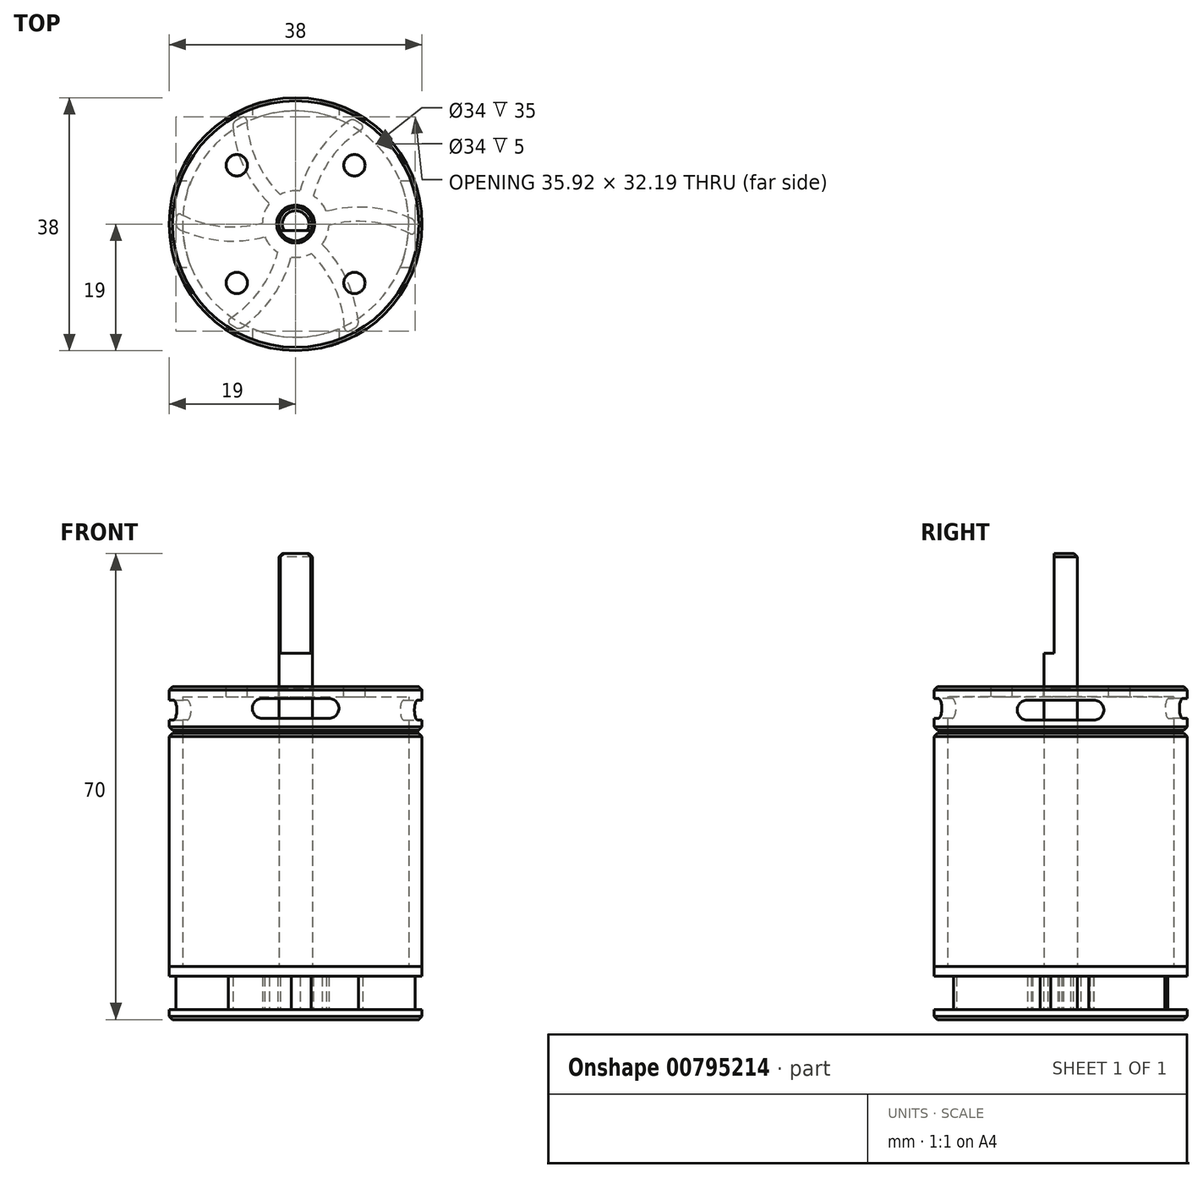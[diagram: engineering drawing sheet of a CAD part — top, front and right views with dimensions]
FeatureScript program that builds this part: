
annotation { "Feature Type Name" : "Feature", "Feature Type Description" : "" }
export const myFeature = defineFeature(function(context is Context, id is Id, definition is map)
    precondition{}
    {
        {
            var Q0;
            Q0=qCreatedBy(makeId("Top.planeOp"),FACE);
            var sketch = newSketch(context, id + "F0", { "sketchPlane" : qUnion([Q0])});
            skCircle(sketch, "E0", {"center": v(0, 0) * mm, "radius": 19 * mm});
            skSolve(sketch);
        }
        {
            var Q0;
            Q0=makeQuery(id+"F0.imprint","IMPRINT",FACE,{"disambiguationData":[TD([[makeQuery(id+"F0.imprint","IMPRINT",EDGE,{"derivedFrom":sQuery(id+"F0.wireOp",EDGE,"E0")}),1.0]])]});
            extrude(context, id + "F1", {"entities" : qUnion([Q0]), "depth" : 1.5 * mm, "offsetDistance" : 25 * mm});
        }
        {
            var Q0;
            Q0=makeQuery(id+"F1.opExtrude","CAP_FACE",FACE,{"disambiguationData":[OSD([sQuery(id+"F0.wireOp",EDGE,"E0")])],"isStart":false});
            var sketch = newSketch(context, id + "F2", { "sketchPlane" : qUnion([Q0])});
            skArc(sketch, "E1", {"start": v(0.66, 4.96) * mm, "mid": v(-0.88, 4.92) * mm, "end": v(-2.33, 4.43) * mm});
            skArc(sketch, "E2.trimOffspring", {"start": v(9.86, 15.01) * mm, "mid": v(9.43, 15.28) * mm, "end": v(9, 15.54) * mm});
            skArc(sketch, "E3.trimOffspring", {"start": v(9.85, 14.17) * mm, "mid": v(5.32, 9.88) * mm, "end": v(2.67, 4.23) * mm});
            skArc(sketch, "E4.trimOffspring", {"start": v(8, 15.5) * mm, "mid": v(3.41, 10.87) * mm, "end": v(0.66, 4.96) * mm});
            skPoint(sketch, "E5.visualSharp", {"position": v(8.49, 15.83) * mm});
            skArc(sketch, "E5.filletArc", {"start": v(9, 15.54) * mm, "mid": v(8.5, 15.67) * mm, "end": v(8, 15.5) * mm});
            skPoint(sketch, "E6.visualSharp", {"position": v(10.5, 14.57) * mm});
            skArc(sketch, "E6.filletArc", {"start": v(9.85, 14.17) * mm, "mid": v(10.08, 14.6) * mm, "end": v(9.86, 15.01) * mm});
            skPoint(sketch, "E7.1.0", {"position": v(-9.46, 15.26) * mm});
            skArc(sketch, "E7.1.1", {"start": v(-9.42, 14.68) * mm, "mid": v(-7.7, 8.4) * mm, "end": v(-3.96, 3.05) * mm});
            skPoint(sketch, "E7.1.2", {"position": v(-7.37, 16.38) * mm});
            skArc(sketch, "E7.1.3", {"start": v(-7.35, 15.62) * mm, "mid": v(-5.9, 9.55) * mm, "end": v(-2.33, 4.43) * mm});
            skArc(sketch, "E7.1.4", {"start": v(-7.35, 15.62) * mm, "mid": v(-7.6, 16.03) * mm, "end": v(-8.07, 16.04) * mm});
            skArc(sketch, "E7.1.5", {"start": v(-8.96, 15.56) * mm, "mid": v(-9.32, 15.19) * mm, "end": v(-9.42, 14.68) * mm});
            skArc(sketch, "E7.1.6", {"start": v(-8.07, 16.04) * mm, "mid": v(-8.52, 15.8) * mm, "end": v(-8.96, 15.56) * mm});
            skPoint(sketch, "E7.2.0", {"position": v(-17.95, -0.56) * mm});
            skArc(sketch, "E7.2.1", {"start": v(-17.43, -0.81) * mm, "mid": v(-11.12, -2.48) * mm, "end": v(-4.62, -1.9) * mm});
            skPoint(sketch, "E7.2.2", {"position": v(-17.87, 1.8) * mm});
            skArc(sketch, "E7.2.3", {"start": v(-17.2, 1.45) * mm, "mid": v(-11.22, -0.33) * mm, "end": v(-5, 0.2) * mm});
            skArc(sketch, "E7.2.4", {"start": v(-17.2, 1.45) * mm, "mid": v(-17.68, 1.43) * mm, "end": v(-17.93, 1.03) * mm});
            skArc(sketch, "E7.2.5", {"start": v(-17.96, 0.02) * mm, "mid": v(-17.81, -0.48) * mm, "end": v(-17.43, -0.81) * mm});
            skArc(sketch, "E7.2.6", {"start": v(-17.93, 1.03) * mm, "mid": v(-17.95, 0.52) * mm, "end": v(-17.96, 0.02) * mm});
            skPoint(sketch, "E7.3.0", {"position": v(-8.49, -15.83) * mm});
            skArc(sketch, "E7.3.1", {"start": v(-8, -15.5) * mm, "mid": v(-3.41, -10.87) * mm, "end": v(-0.66, -4.96) * mm});
            skPoint(sketch, "E7.3.2", {"position": v(-10.5, -14.57) * mm});
            skArc(sketch, "E7.3.3", {"start": v(-9.85, -14.17) * mm, "mid": v(-5.32, -9.88) * mm, "end": v(-2.67, -4.23) * mm});
            skArc(sketch, "E7.3.4", {"start": v(-9.85, -14.17) * mm, "mid": v(-10.08, -14.6) * mm, "end": v(-9.86, -15.01) * mm});
            skArc(sketch, "E7.3.5", {"start": v(-9, -15.54) * mm, "mid": v(-8.5, -15.67) * mm, "end": v(-8, -15.5) * mm});
            skArc(sketch, "E7.3.6", {"start": v(-9.86, -15.01) * mm, "mid": v(-9.43, -15.28) * mm, "end": v(-9, -15.54) * mm});
            skPoint(sketch, "E7.4.0", {"position": v(9.46, -15.26) * mm});
            skArc(sketch, "E7.4.1", {"start": v(9.42, -14.68) * mm, "mid": v(7.7, -8.4) * mm, "end": v(3.96, -3.05) * mm});
            skPoint(sketch, "E7.4.2", {"position": v(7.37, -16.38) * mm});
            skArc(sketch, "E7.4.3", {"start": v(7.35, -15.62) * mm, "mid": v(5.9, -9.55) * mm, "end": v(2.33, -4.43) * mm});
            skArc(sketch, "E7.4.4", {"start": v(7.35, -15.62) * mm, "mid": v(7.6, -16.03) * mm, "end": v(8.07, -16.04) * mm});
            skArc(sketch, "E7.4.5", {"start": v(8.96, -15.56) * mm, "mid": v(9.32, -15.19) * mm, "end": v(9.42, -14.68) * mm});
            skArc(sketch, "E7.4.6", {"start": v(8.07, -16.04) * mm, "mid": v(8.52, -15.8) * mm, "end": v(8.96, -15.56) * mm});
            skPoint(sketch, "E7.5.0", {"position": v(17.95, 0.56) * mm});
            skArc(sketch, "E7.5.1", {"start": v(17.43, 0.81) * mm, "mid": v(11.12, 2.48) * mm, "end": v(4.62, 1.9) * mm});
            skPoint(sketch, "E7.5.2", {"position": v(17.87, -1.8) * mm});
            skArc(sketch, "E7.5.3", {"start": v(17.2, -1.45) * mm, "mid": v(11.22, 0.33) * mm, "end": v(5, -0.2) * mm});
            skArc(sketch, "E7.5.4", {"start": v(17.2, -1.45) * mm, "mid": v(17.68, -1.43) * mm, "end": v(17.93, -1.03) * mm});
            skArc(sketch, "E7.5.5", {"start": v(17.96, -0.02) * mm, "mid": v(17.81, 0.48) * mm, "end": v(17.43, 0.81) * mm});
            skArc(sketch, "E7.5.6", {"start": v(17.93, -1.03) * mm, "mid": v(17.95, -0.52) * mm, "end": v(17.96, -0.02) * mm});
            skArc(sketch, "E8.trimOffspring", {"start": v(-3.96, 3.05) * mm, "mid": v(-4.7, 1.7) * mm, "end": v(-5, 0.2) * mm});
            skArc(sketch, "E9.trimOffspring", {"start": v(-4.62, -1.9) * mm, "mid": v(-3.83, -3.22) * mm, "end": v(-2.67, -4.23) * mm});
            skArc(sketch, "E10.trimOffspring", {"start": v(-0.66, -4.96) * mm, "mid": v(0.88, -4.92) * mm, "end": v(2.33, -4.43) * mm});
            skArc(sketch, "E11.trimOffspring", {"start": v(3.96, -3.05) * mm, "mid": v(4.7, -1.7) * mm, "end": v(5, -0.2) * mm});
            skArc(sketch, "E12.trimOffspring", {"start": v(4.62, 1.9) * mm, "mid": v(3.83, 3.22) * mm, "end": v(2.67, 4.23) * mm});
            skSolve(sketch);
        }
        {
            var Q0;
            Q0 = qSketchRegion(id + "F2", true);
            extrude(context, id + "F3", {"entities" : qUnion([Q0]), "operationType" : NewBodyOperationType.ADD, "depth" : 5 * mm, "offsetDistance" : 25 * mm});
        }
        {
            var Q0;
            Q0=makeQuery(id+"F3.opExtrude","CAP_FACE",FACE,{"disambiguationData":[OSD([sQuery(id+"F2.wireOp",EDGE,"E1"),sQuery(id+"F2.wireOp",EDGE,"E2.trimOffspring"),sQuery(id+"F2.wireOp",EDGE,"E3.trimOffspring"),sQuery(id+"F2.wireOp",EDGE,"E4.trimOffspring"),sQuery(id+"F2.wireOp",EDGE,"E5.filletArc"),sQuery(id+"F2.wireOp",EDGE,"E6.filletArc"),sQuery(id+"F2.wireOp",EDGE,"E7.1.1"),sQuery(id+"F2.wireOp",EDGE,"E7.1.3"),sQuery(id+"F2.wireOp",EDGE,"E7.1.4"),sQuery(id+"F2.wireOp",EDGE,"E7.1.5"),sQuery(id+"F2.wireOp",EDGE,"E7.1.6"),sQuery(id+"F2.wireOp",EDGE,"E7.2.1"),sQuery(id+"F2.wireOp",EDGE,"E7.2.3"),sQuery(id+"F2.wireOp",EDGE,"E7.2.4"),sQuery(id+"F2.wireOp",EDGE,"E7.2.5"),sQuery(id+"F2.wireOp",EDGE,"E7.2.6"),sQuery(id+"F2.wireOp",EDGE,"E7.3.1"),sQuery(id+"F2.wireOp",EDGE,"E7.3.3"),sQuery(id+"F2.wireOp",EDGE,"E7.3.4"),sQuery(id+"F2.wireOp",EDGE,"E7.3.5"),sQuery(id+"F2.wireOp",EDGE,"E7.3.6"),sQuery(id+"F2.wireOp",EDGE,"E7.4.1"),sQuery(id+"F2.wireOp",EDGE,"E7.4.3"),sQuery(id+"F2.wireOp",EDGE,"E7.4.4"),sQuery(id+"F2.wireOp",EDGE,"E7.4.5"),sQuery(id+"F2.wireOp",EDGE,"E7.4.6"),sQuery(id+"F2.wireOp",EDGE,"E7.5.1"),sQuery(id+"F2.wireOp",EDGE,"E7.5.3"),sQuery(id+"F2.wireOp",EDGE,"E7.5.4"),sQuery(id+"F2.wireOp",EDGE,"E7.5.5"),sQuery(id+"F2.wireOp",EDGE,"E7.5.6"),sQuery(id+"F2.wireOp",EDGE,"E8.trimOffspring"),sQuery(id+"F2.wireOp",EDGE,"E9.trimOffspring"),sQuery(id+"F2.wireOp",EDGE,"E10.trimOffspring"),sQuery(id+"F2.wireOp",EDGE,"E11.trimOffspring"),sQuery(id+"F2.wireOp",EDGE,"E12.trimOffspring")])],"isStart":false});
            var sketch = newSketch(context, id + "F4", { "sketchPlane" : qUnion([Q0])});
            skCircle(sketch, "E13", {"center": v(0, 0) * mm, "radius": 19 * mm});
            skSolve(sketch);
        }
        {
            var Q0;
            Q0 = qSketchRegion(id + "F4", true);
            extrude(context, id + "F5", {"entities" : qUnion([Q0]), "operationType" : NewBodyOperationType.ADD, "depth" : 1.5 * mm, "offsetDistance" : 25 * mm});
        }
        {
            var Q0;
            Q0=makeQuery(id+"F1.opExtrude","CAP_EDGE",EDGE,{"disambiguationData":[OSD([sQuery(id+"F0.wireOp",EDGE,"E0")])],"isStart":true});
            chamfer(context, id + "F6", {"entities" : qUnion([Q0]), "width" : .5 * mm, "tangentPropagation" : true});
        }
        {
            var Q0;
            Q0=makeQuery(id+"F5.opExtrude","CAP_FACE",FACE,{"disambiguationData":[OSD([sQuery(id+"F4.wireOp",EDGE,"E13")])],"isStart":false});
            var sketch = newSketch(context, id + "F7", { "sketchPlane" : qUnion([Q0])});
            skCircle(sketch, "E14", {"center": v(0, 0) * mm, "radius": 19 * mm});
            skCircle(sketch, "E15", {"center": v(0, 0) * mm, "radius": 17 * mm});
            skSolve(sketch);
        }
        {
            var Q0;
            Q0 = qSketchRegion(id + "F7", true);
            extrude(context, id + "F8", {"entities" : qUnion([Q0]), "depth" : 35 * mm, "offsetDistance" : 25 * mm});
        }
        {
            var Q0;
            Q0=makeQuery(id+"F8.opExtrude","CAP_FACE",FACE,{"disambiguationData":[OSD([sQuery(id+"F7.wireOp",EDGE,"E14"),sQuery(id+"F7.wireOp",EDGE,"E15")])],"isStart":false});
            cPlane(context, id + "F9", {"entities" : qUnion([Q0]), "cplaneType" : CPlaneType.OFFSET, "offset" : .5 * mm, "width" : 150 * mm, "height" : 150 * mm});
        }
        {
            var Q0;
            Q0=qCreatedBy(id+"F9.planeOp",FACE);
            var sketch = newSketch(context, id + "F10", { "sketchPlane" : qUnion([Q0])});
            skCircle(sketch, "E16", {"center": v(0, 0) * mm, "radius": 19 * mm});
            skSolve(sketch);
        }
        {
            var Q0;
            Q0 = qSketchRegion(id + "F10", true);
            extrude(context, id + "F11", {"entities" : qUnion([Q0]), "depth" : 6.5 * mm, "offsetDistance" : 25 * mm});
        }
        {
            var Q0;
            Q0=makeQuery(id+"F8.opExtrude","CAP_EDGE",EDGE,{"disambiguationData":[OSD([sQuery(id+"F7.wireOp",EDGE,"E14")])],"isStart":false});
            var Q1;
            Q1=makeQuery(id+"F11.opExtrude","CAP_EDGE",EDGE,{"disambiguationData":[OSD([sQuery(id+"F10.wireOp",EDGE,"E16")])],"isStart":true});
            var Q2;
            Q2=makeQuery(id+"F11.opExtrude","CAP_EDGE",EDGE,{"disambiguationData":[OSD([sQuery(id+"F10.wireOp",EDGE,"E16")])],"isStart":false});
            chamfer(context, id + "F12", {"entities" : qUnion([Q0, Q1, Q2]), "width" : .5 * mm, "tangentPropagation" : true});
        }
        {
            var Q0;
            Q0=qCreatedBy(makeId("Front.planeOp"),FACE);
            var sketch = newSketch(context, id + "F13", { "sketchPlane" : qUnion([Q0])});
            skLineSegment(sketch, "E17", {"start": v(-5, 46.75) * mm, "end": v(5, 46.75) * mm, "construction": true});
            skArc(sketch, "E18.0.startCap", {"start": v(-5, 45.25) * mm, "mid": v(-6.5, 46.75) * mm, "end": v(-5, 48.25) * mm});
            skArc(sketch, "E18.0.endCap", {"start": v(5, 48.25) * mm, "mid": v(6.5, 46.75) * mm, "end": v(5, 45.25) * mm});
            skLineSegment(sketch, "E18.0.left", {"start": v(-5, 48.25) * mm, "end": v(5, 48.25) * mm});
            skLineSegment(sketch, "E18.0.right", {"start": v(-5, 45.25) * mm, "end": v(5, 45.25) * mm});
            skSolve(sketch);
        }
        {
            var Q0;
            Q0 = qSketchRegion(id + "F13", true);
            extrude(context, id + "F14", {"entities" : qUnion([Q0]), "operationType" : NewBodyOperationType.REMOVE, "endBound" : BoundingType.SYMMETRIC, "oppositeDirection" : true, "depth" : 75 * mm, "offsetDistance" : 25 * mm});
        }
        {
            var Q0;
            Q0=qCreatedBy(makeId("Right.planeOp"),FACE);
            var sketch = newSketch(context, id + "F15", { "sketchPlane" : qUnion([Q0])});
            skLineSegment(sketch, "E19", {"start": v(5, 46.5) * mm, "end": v(-5, 46.5) * mm});
            skArc(sketch, "E20.0.startCap", {"start": v(5, 48) * mm, "mid": v(6.5, 46.5) * mm, "end": v(5, 45) * mm});
            skArc(sketch, "E20.0.endCap", {"start": v(-5, 45) * mm, "mid": v(-6.5, 46.5) * mm, "end": v(-5, 48) * mm});
            skLineSegment(sketch, "E20.0.left", {"start": v(5, 45) * mm, "end": v(-5, 45) * mm});
            skLineSegment(sketch, "E20.0.right", {"start": v(5, 48) * mm, "end": v(-5, 48) * mm});
            skSolve(sketch);
        }
        {
            var Q0;
            Q0 = qSketchRegion(id + "F15", true);
            extrude(context, id + "F16", {"entities" : qUnion([Q0]), "operationType" : NewBodyOperationType.REMOVE, "endBound" : BoundingType.SYMMETRIC, "oppositeDirection" : true, "depth" : 75 * mm, "offsetDistance" : 25 * mm});
        }
        {
            var Q0;
            Q0=makeQuery(id+"F11.opExtrude","CAP_FACE",FACE,{"disambiguationData":[OSD([sQuery(id+"F10.wireOp",EDGE,"E16")])],"isStart":true});
            var sketch = newSketch(context, id + "F17", { "sketchPlane" : qUnion([Q0])});
            skCircle(sketch, "E21", {"center": v(0, 0) * mm, "radius": 17 * mm});
            skSolve(sketch);
        }
        {
            var Q0;
            Q0=makeQuery(id+"F17.imprint","IMPRINT",FACE,{"disambiguationData":[TD([[makeQuery(id+"F17.imprint","IMPRINT",EDGE,{"derivedFrom":sQuery(id+"F17.wireOp",EDGE,"E21")}),1.0]])]});
            extrude(context, id + "F18", {"entities" : qUnion([Q0]), "operationType" : NewBodyOperationType.REMOVE, "oppositeDirection" : true, "depth" : 5 * mm, "offsetDistance" : 25 * mm});
        }
        {
            var Q0;
            Q0=makeQuery(id+"F5.opExtrude","CAP_FACE",FACE,{"disambiguationData":[OSD([sQuery(id+"F4.wireOp",EDGE,"E13")])],"isStart":false});
            var sketch = newSketch(context, id + "F19", { "sketchPlane" : qUnion([Q0])});
            skCircle(sketch, "E22", {"center": v(0, 0) * mm, "radius": 2.6 * mm});
            skSolve(sketch);
        }
        {
            var Q0;
            Q0=makeQuery(id+"F19.imprint","IMPRINT",FACE,{"disambiguationData":[TD([[makeQuery(id+"F19.imprint","IMPRINT",EDGE,{"derivedFrom":sQuery(id+"F19.wireOp",EDGE,"E22")}),1.0]])]});
            extrude(context, id + "F20", {"entities" : qUnion([Q0]), "operationType" : NewBodyOperationType.REMOVE, "depth" : 45 * mm, "offsetDistance" : 25 * mm});
        }
        {
            var Q0;
            Q0=makeQuery(id+"F20.boolean.opBoolean","INTERSECT",EDGE,{"derivedFrom":[makeQuery(id+"F11.opExtrude","CAP_FACE",FACE,{"disambiguationData":[OSD([sQuery(id+"F10.wireOp",EDGE,"E16")])],"isStart":false}),makeQuery(id+"F20.opExtrude","SWEPT_FACE",FACE,{"disambiguationData":[OSD([sQuery(id+"F19.wireOp",EDGE,"E22")])]})]});
            chamfer(context, id + "F21", {"entities" : qUnion([Q0]), "width" : .25 * mm, "tangentPropagation" : true});
        }
        {
            var Q0;
            Q0=makeQuery(id+"F5.opExtrude","CAP_FACE",FACE,{"disambiguationData":[OSD([sQuery(id+"F4.wireOp",EDGE,"E13")])],"isStart":false});
            var sketch = newSketch(context, id + "F22", { "sketchPlane" : qUnion([Q0])});
            skCircle(sketch, "E23", {"center": v(0, 0) * mm, "radius": 2.5 * mm});
            skSolve(sketch);
        }
        {
            var Q0;
            Q0=makeQuery(id+"F22.imprint","IMPRINT",FACE,{"disambiguationData":[TD([[makeQuery(id+"F22.imprint","IMPRINT",EDGE,{"derivedFrom":sQuery(id+"F22.wireOp",EDGE,"E23")}),1.0]])]});
            extrude(context, id + "F23", {"entities" : qUnion([Q0]), "depth" : 62 * mm, "offsetDistance" : 25 * mm});
        }
        {
            var Q0;
            Q0=makeQuery(id+"F23.opExtrude","CAP_FACE",FACE,{"disambiguationData":[OSD([sQuery(id+"F22.wireOp",EDGE,"E23")])],"isStart":false});
            var sketch = newSketch(context, id + "F24", { "sketchPlane" : qUnion([Q0])});
            skLineSegment(sketch, "E24", {"start": v(-2.5, -1) * mm, "end": v(2.72, -1) * mm});
            skSolve(sketch);
        }
        {
            var Q0;
            Q0=makeQuery(id+"F23.opExtrude","CAP_EDGE",EDGE,{"disambiguationData":[OSD([sQuery(id+"F22.wireOp",EDGE,"E23")])],"isStart":false});
            chamfer(context, id + "F25", {"entities" : qUnion([Q0]), "width" : .5 * mm, "tangentPropagation" : true});
        }
        {
            var Q0;
            {var subQ0=sQuery(id+"F24.wireOp",EDGE,"E24");var subQ1=makeQuery(id+"F23.opExtrude","CAP_EDGE",EDGE,{"disambiguationData":[OSD([sQuery(id+"F22.wireOp",EDGE,"E23")])],"isStart":false});var subQ2=makeQuery(id+"F24.imprint","INTERSECT",VERTEX,{"disambiguationData":[OD(0.0)],"derivedFrom":[subQ1,subQ0]});Q0=makeQuery(id+"F24.imprint","IMPRINT",FACE,{"disambiguationData":[TD([[makeQuery(id+"F24.imprint","IMPRINT",EDGE,{"disambiguationData":[TD([[subQ2,-1.0]])],"derivedFrom":subQ0}),-1.0]])]});}
            extrude(context, id + "F26", {"entities" : qUnion([Q0]), "operationType" : NewBodyOperationType.REMOVE, "oppositeDirection" : true, "depth" : 15 * mm, "offsetDistance" : 25 * mm});
        }
        {
            var Q0;
            {var subQ0=sQuery(id+"F24.wireOp",EDGE,"E24");var subQ1=makeQuery(id+"F23.opExtrude","CAP_EDGE",EDGE,{"disambiguationData":[OSD([sQuery(id+"F22.wireOp",EDGE,"E23")])],"isStart":false});var subQ2=makeQuery(id+"F24.imprint","INTERSECT",VERTEX,{"disambiguationData":[OD(0.0)],"derivedFrom":[subQ1,subQ0]});Q0=makeQuery(id+"F24.imprint","IMPRINT",FACE,{"disambiguationData":[TD([[makeQuery(id+"F24.imprint","IMPRINT",EDGE,{"disambiguationData":[TD([[subQ2,-1.0]])],"derivedFrom":subQ0}),-1.0]])]});}
            extrude(context, id + "F27", {"entities" : qUnion([Q0]), "operationType" : NewBodyOperationType.REMOVE, "oppositeDirection" : true, "depth" : 15 * mm, "offsetDistance" : 25 * mm});
        }
        {
            var Q0;
            Q0=makeQuery(id+"F11.opExtrude","CAP_FACE",FACE,{"disambiguationData":[OSD([sQuery(id+"F10.wireOp",EDGE,"E16")])],"isStart":false});
            var sketch = newSketch(context, id + "F28", { "sketchPlane" : qUnion([Q0])});
            skCircle(sketch, "E25", {"center": v(0, 0) * mm, "radius": 12.5 * mm, "construction": true});
            skLineSegment(sketch, "E26", {"start": v(0, 0) * mm, "end": v(-11.57, 11.57) * mm, "construction": true});
            skCircle(sketch, "E27", {"center": v(-8.84, 8.84) * mm, "radius": 1.6 * mm});
            skCircle(sketch, "E28.1.0", {"center": v(-8.84, -8.84) * mm, "radius": 1.6 * mm});
            skCircle(sketch, "E28.2.0", {"center": v(8.84, -8.84) * mm, "radius": 1.6 * mm});
            skCircle(sketch, "E28.3.0", {"center": v(8.84, 8.84) * mm, "radius": 1.6 * mm});
            skSolve(sketch);
        }
        {
            var Q0;
            Q0 = qSketchRegion(id + "F28", true);
            extrude(context, id + "F29", {"entities" : qUnion([Q0]), "operationType" : NewBodyOperationType.REMOVE, "oppositeDirection" : true, "depth" : 4 * mm, "offsetDistance" : 25 * mm});
        }
    });
